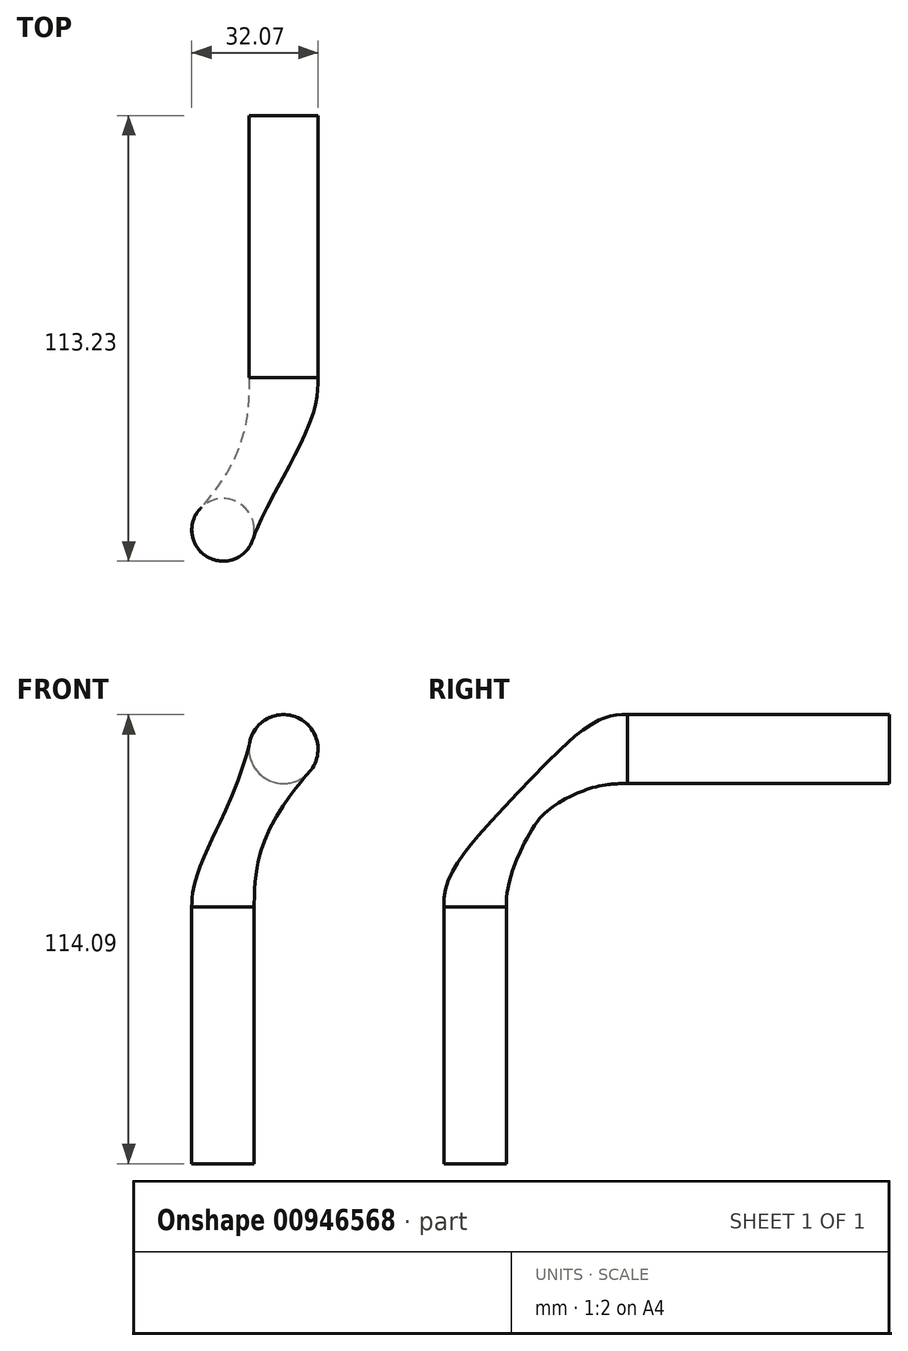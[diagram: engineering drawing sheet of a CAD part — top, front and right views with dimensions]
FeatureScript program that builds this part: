
annotation { "Feature Type Name" : "Feature", "Feature Type Description" : "" }
export const myFeature = defineFeature(function(context is Context, id is Id, definition is map)
    precondition{}
    {
        {
            var Q0;
            Q0=qCreatedBy(makeId("Top.planeOp"),FACE);
            var sketch = newSketch(context, id + "F0", { "sketchPlane" : qUnion([Q0])});
            skCircle(sketch, "E0", {"center": v(-70.73, -38.74) * mm, "radius": 7.94 * mm});
            skSolve(sketch);
        }
        {
            var Q0;
            Q0 = qSketchRegion(id + "F0", true);
            extrude(context, id + "F1", {"entities" : qUnion([Q0]), "oppositeDirection" : true, "depth" : 65.28 * mm, "offsetDistance" : 25.4 * mm});
        }
        {
            var Q0;
            Q0=qCreatedBy(makeId("Front.planeOp"),FACE);
            var sketch = newSketch(context, id + "F2", { "sketchPlane" : qUnion([Q0])});
            skCircle(sketch, "E1", {"center": v(-55.35, 40.05) * mm, "radius": 8.76 * mm});
            skSolve(sketch);
        }
        {
            var Q0;
            Q0 = qSketchRegion(id + "F2", true);
            extrude(context, id + "F3", {"entities" : qUnion([Q0]), "oppositeDirection" : true, "depth" : 66.55 * mm, "offsetDistance" : 25.4 * mm});
        }
        {
            var Q0;
            Q0=makeQuery(id+"F1.opExtrude","CAP_FACE",FACE,{"disambiguationData":[OSD([sQuery(id+"F0.wireOp",EDGE,"E0")])],"isStart":true});
            var Q1;
            Q1=makeQuery(id+"F3.opExtrude","CAP_FACE",FACE,{"disambiguationData":[OSD([sQuery(id+"F2.wireOp",EDGE,"E1")])],"isStart":true});
            loft(context, id + "F4", {"startCondition" : LoftEndDerivativeType.MATCH_CURVATURE, "startMagnitude" : 1, "endCondition" : LoftEndDerivativeType.MATCH_CURVATURE, "endMagnitude" : 1, "sheetProfilesArray" : [{ "sheetProfileEntities" : qUnion([Q0]) }, { "sheetProfileEntities" : qUnion([Q1]) }]});
        }
    });
